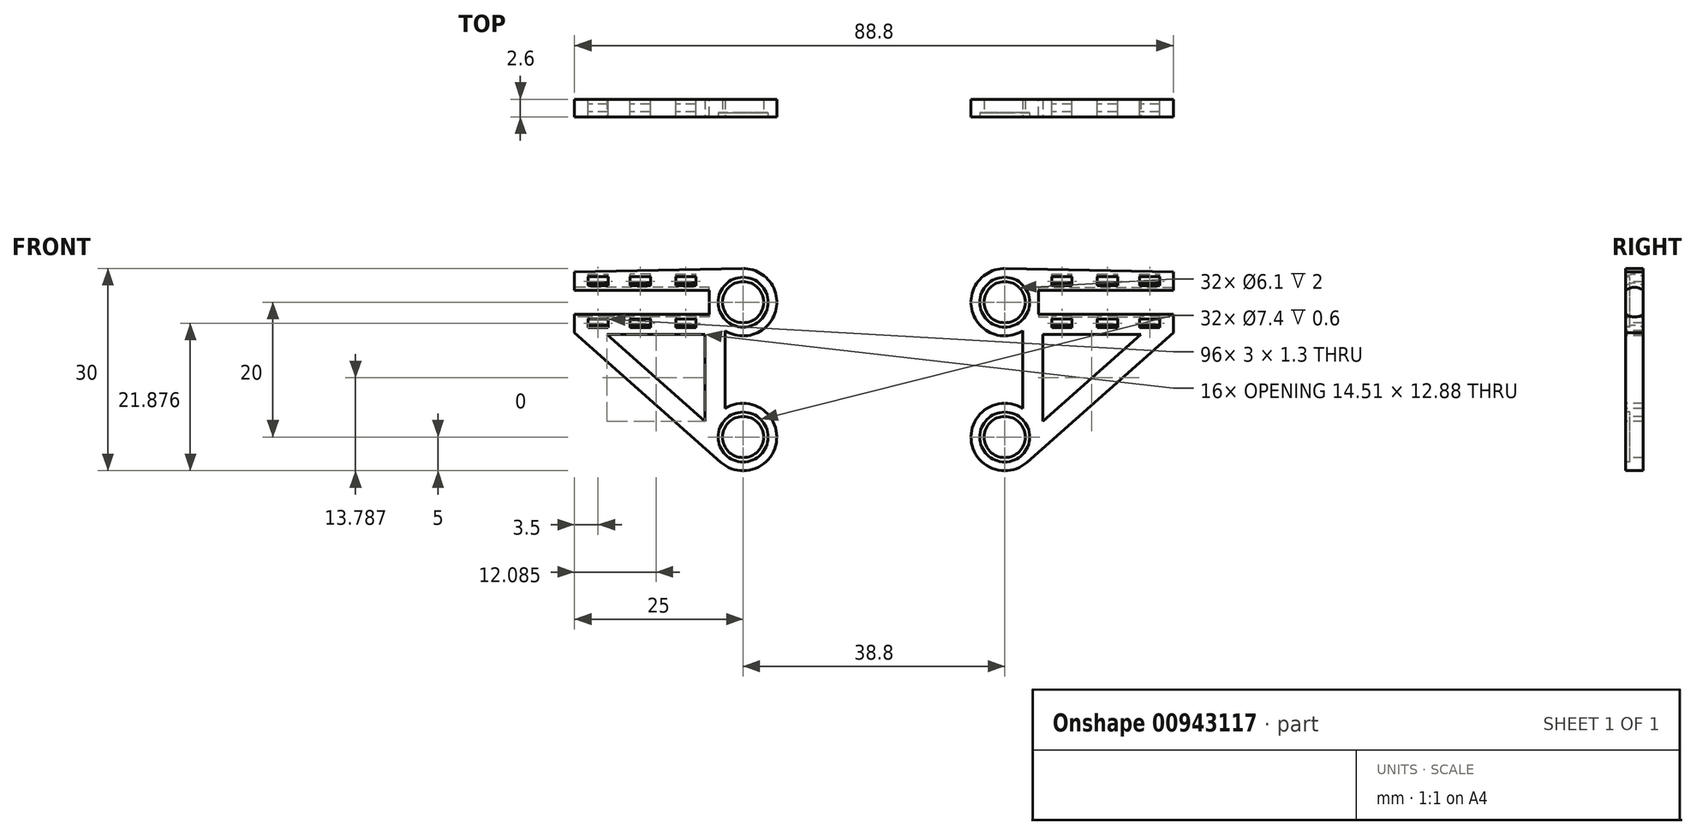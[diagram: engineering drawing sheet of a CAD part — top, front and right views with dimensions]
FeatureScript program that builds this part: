
annotation { "Feature Type Name" : "Feature", "Feature Type Description" : "" }
export const myFeature = defineFeature(function(context is Context, id is Id, definition is map)
    precondition{}
    {
        {
            var Q0;
            Q0=qCreatedBy(makeId("Front.planeOp"),FACE);
            var sketch = newSketch(context, id + "F0", { "sketchPlane" : qUnion([Q0])});
            skLineSegment(sketch, "E0", {"start": v(0.1, 5) * mm, "end": v(25, 4.5) * mm});
            skLineSegment(sketch, "E1", {"start": v(25, 4.5) * mm, "end": v(25, -4.5) * mm});
            skLineSegment(sketch, "E2", {"start": v(25, -4.5) * mm, "end": v(3.32, -23.74) * mm});
            skPoint(sketch, "E3", {"position": v(0, 0) * mm});
            skPoint(sketch, "E4", {"position": v(0, -20) * mm});
            skLineSegment(sketch, "E5", {"start": v(0, 0) * mm, "end": v(25, 0) * mm, "construction": true});
            skArc(sketch, "E6.filletArc", {"start": v(2.66, -15.77) * mm, "mid": v(-4.98, -20.41) * mm, "end": v(3.32, -23.74) * mm});
            skArc(sketch, "E7.filletArc", {"start": v(0.1, 5) * mm, "mid": v(-4.82, -1.34) * mm, "end": v(2.66, -4.23) * mm});
            skLineSegment(sketch, "E8", {"start": v(2.66, -4.23) * mm, "end": v(2.66, -15.77) * mm});
            skSolve(sketch);
        }
        {
            var Q0;
            Q0=makeQuery(id+"F0.imprint","IMPRINT",FACE,{"disambiguationData":[TD([[makeQuery(id+"F0.imprint","IMPRINT",EDGE,{"derivedFrom":sQuery(id+"F0.wireOp",EDGE,"E0")}),-1.0]])]});
            extrude(context, id + "F1", {"entities" : qUnion([Q0]), "oppositeDirection" : true, "depth" : 2.6 * mm, "offsetDistance" : 25 * mm});
        }
        {
            var Q0;
            Q0=sQuery(id+"F0.wireOp",VERTEX,"E3");
            var Q1;
            Q1=sQuery(id+"F0.wireOp",VERTEX,"E4");
            var Q2;
            Q2=makeQuery(id+"F1.opExtrude","SWEPT_BODY",BODY,{"disambiguationData":[OSD([sQuery(id+"F0.wireOp",EDGE,"RJbdalpD-36lB-MyLH-ccrA-Tx8w9Rtr1OP7"),sQuery(id+"F0.wireOp",EDGE,"E0"),sQuery(id+"F0.wireOp",EDGE,"E1"),sQuery(id+"F0.wireOp",EDGE,"E2"),sQuery(id+"F0.wireOp",EDGE,"E6.filletArc"),sQuery(id+"F0.wireOp",EDGE,"E7.filletArc")])]});
            hole(context, id + "F2", {"style" : HoleStyle.C_BORE, "endStyle" : HoleEndStyle.BLIND, "holeDiameter" : 6.1 * mm, "cBoreDiameter" : 7.4 * mm, "cBoreDepth" : 0.6 * mm, "majorDiameter" : 5 * mm, "holeDepth" : 3 * mm, "isTappedThrough" : true, "tappedDepth" : 12 * mm, "tapClearance" : 3, "startFromSketch" : true, "locations" : qUnion([Q0, Q1]), "scope" : qUnion([Q2])});
        }
        {
            var Q0;
            Q0=makeQuery(id+"F1.opExtrude","SWEPT_FACE",FACE,{"disambiguationData":[OSD([sQuery(id+"F0.wireOp",EDGE,"E1")])]});
            var sketch = newSketch(context, id + "F3", { "sketchPlane" : qUnion([Q0])});
            skCircle(sketch, "E9", {"center": v(1.3, 0) * mm, "radius": 2.2 * mm});
            skPoint(sketch, "E9.centerSnap0", {"position": v(1.3, 4.5) * mm});
            skPoint(sketch, "E9.centerSnap1", {"position": v(2.6, 0) * mm});
            skSolve(sketch);
        }
        {
            var Q0;
            Q0=qSketchRegion(id+"F3",true);
            extrude(context, id + "F4", {"entities" : qUnion([Q0]), "operationType" : NewBodyOperationType.REMOVE, "oppositeDirection" : true, "depth" : 20 * mm, "offsetDistance" : 25 * mm});
        }
        {
            var Q0;
            Q0=qCreatedBy(makeId("Front.planeOp"),FACE);
            var sketch = newSketch(context, id + "F5", { "sketchPlane" : qUnion([Q0])});
            skLineSegment(sketch, "E10", {"start": v(5.66, -4.77) * mm, "end": v(5.66, -17.65) * mm});
            skLineSegment(sketch, "E11", {"start": v(5.66, -17.65) * mm, "end": v(20.17, -4.77) * mm});
            skLineSegment(sketch, "E12", {"start": v(20.17, -4.77) * mm, "end": v(5.66, -4.77) * mm});
            skSolve(sketch);
        }
        {
            var Q0;
            Q0=qSketchRegion(id+"F5",true);
            extrude(context, id + "F6", {"entities" : qUnion([Q0]), "operationType" : NewBodyOperationType.REMOVE, "oppositeDirection" : true, "depth" : 25 * mm, "offsetDistance" : 25 * mm});
        }
        {
            var Q0;
            Q0=makeQuery(id+"F1.opExtrude","CAP_FACE",FACE,{"disambiguationData":[OSD([sQuery(id+"F0.wireOp",EDGE,"E0"),sQuery(id+"F0.wireOp",EDGE,"E1"),sQuery(id+"F0.wireOp",EDGE,"E2"),sQuery(id+"F0.wireOp",EDGE,"E6.filletArc"),sQuery(id+"F0.wireOp",EDGE,"E7.filletArc"),sQuery(id+"F0.wireOp",EDGE,"E8")])],"isStart":true});
            var sketch = newSketch(context, id + "F7", { "sketchPlane" : qUnion([Q0])});
            skLineSegment(sketch, "E13.bottom", {"start": v(20, 3.77) * mm, "end": v(23, 3.77) * mm});
            skLineSegment(sketch, "E13.top", {"start": v(20, 2.47) * mm, "end": v(23, 2.47) * mm});
            skLineSegment(sketch, "E13.left", {"start": v(20, 3.77) * mm, "end": v(20, 2.47) * mm});
            skLineSegment(sketch, "E13.right", {"start": v(23, 3.77) * mm, "end": v(23, 2.47) * mm});
            skLineSegment(sketch, "E14.bottom", {"start": v(7, 3.77) * mm, "end": v(10, 3.77) * mm});
            skLineSegment(sketch, "E14.top", {"start": v(7, 2.47) * mm, "end": v(10, 2.47) * mm});
            skLineSegment(sketch, "E14.left", {"start": v(7, 3.77) * mm, "end": v(7, 2.47) * mm});
            skLineSegment(sketch, "E14.right", {"start": v(10, 3.77) * mm, "end": v(10, 2.47) * mm});
            skLineSegment(sketch, "E15.bottom", {"start": v(7, -2.47) * mm, "end": v(10, -2.47) * mm});
            skLineSegment(sketch, "E15.top", {"start": v(7, -3.77) * mm, "end": v(10, -3.77) * mm});
            skLineSegment(sketch, "E15.left", {"start": v(7, -2.47) * mm, "end": v(7, -3.77) * mm});
            skLineSegment(sketch, "E15.right", {"start": v(10, -2.47) * mm, "end": v(10, -3.77) * mm});
            skLineSegment(sketch, "E16.bottom", {"start": v(20, -2.47) * mm, "end": v(23, -2.47) * mm});
            skLineSegment(sketch, "E16.top", {"start": v(20, -3.77) * mm, "end": v(23, -3.77) * mm});
            skLineSegment(sketch, "E16.left", {"start": v(20, -2.47) * mm, "end": v(20, -3.77) * mm});
            skLineSegment(sketch, "E16.right", {"start": v(23, -2.47) * mm, "end": v(23, -3.77) * mm});
            skLineSegment(sketch, "E17.bottom", {"start": v(13.74, 3.77) * mm, "end": v(16.74, 3.77) * mm});
            skLineSegment(sketch, "E17.top", {"start": v(13.74, 2.47) * mm, "end": v(16.74, 2.47) * mm});
            skLineSegment(sketch, "E17.left", {"start": v(13.74, 3.77) * mm, "end": v(13.74, 2.47) * mm});
            skLineSegment(sketch, "E17.right", {"start": v(16.74, 3.77) * mm, "end": v(16.74, 2.47) * mm});
            skLineSegment(sketch, "E18.bottom", {"start": v(13.74, -2.47) * mm, "end": v(16.74, -2.47) * mm});
            skLineSegment(sketch, "E18.top", {"start": v(13.74, -3.77) * mm, "end": v(16.74, -3.77) * mm});
            skLineSegment(sketch, "E18.left", {"start": v(13.74, -2.47) * mm, "end": v(13.74, -3.77) * mm});
            skLineSegment(sketch, "E18.right", {"start": v(16.74, -2.47) * mm, "end": v(16.74, -3.77) * mm});
            skSolve(sketch);
        }
        {
            var Q0;
            Q0=makeQuery(id+"F7.imprint","IMPRINT",FACE,{"disambiguationData":[TD([[makeQuery(id+"F7.imprint","IMPRINT",EDGE,{"derivedFrom":sQuery(id+"F7.wireOp",EDGE,"E14.bottom")}),-1.0]])]});
            var Q1;
            Q1=makeQuery(id+"F7.imprint","IMPRINT",FACE,{"disambiguationData":[TD([[makeQuery(id+"F7.imprint","IMPRINT",EDGE,{"derivedFrom":sQuery(id+"F7.wireOp",EDGE,"E17.bottom")}),-1.0]])]});
            var Q2;
            Q2=makeQuery(id+"F7.imprint","IMPRINT",FACE,{"disambiguationData":[TD([[makeQuery(id+"F7.imprint","IMPRINT",EDGE,{"derivedFrom":sQuery(id+"F7.wireOp",EDGE,"E13.bottom")}),-1.0]])]});
            var Q3;
            Q3=makeQuery(id+"F4.boolean.opBoolean","COPY",EDGE,{"disambiguationData":[OD(0.0)],"derivedFrom":makeQuery(id+"F4.opExtrude","CAP_EDGE",EDGE,{"disambiguationData":[OSD([sQuery(id+"F3.wireOp",EDGE,"E9")])],"isStart":true})});
            sweep(context, id + "F8", {"operationType" : NewBodyOperationType.REMOVE, "profiles" : qUnion([Q0, Q1, Q2]), "path" : qUnion([Q3]), "keepProfileOrientation" : true});
        }
        {
            var Q0;
            Q0=makeQuery(id+"F7.imprint","IMPRINT",FACE,{"disambiguationData":[TD([[makeQuery(id+"F7.imprint","IMPRINT",EDGE,{"derivedFrom":sQuery(id+"F7.wireOp",EDGE,"E15.bottom")}),-1.0]])]});
            var Q1;
            Q1=makeQuery(id+"F7.imprint","IMPRINT",FACE,{"disambiguationData":[TD([[makeQuery(id+"F7.imprint","IMPRINT",EDGE,{"derivedFrom":sQuery(id+"F7.wireOp",EDGE,"E18.bottom")}),-1.0]])]});
            var Q2;
            Q2=makeQuery(id+"F7.imprint","IMPRINT",FACE,{"disambiguationData":[TD([[makeQuery(id+"F7.imprint","IMPRINT",EDGE,{"derivedFrom":sQuery(id+"F7.wireOp",EDGE,"E16.bottom")}),-1.0]])]});
            var Q3;
            Q3=makeQuery(id+"F4.boolean.opBoolean","COPY",EDGE,{"disambiguationData":[OD(1.0)],"derivedFrom":makeQuery(id+"F4.opExtrude","CAP_EDGE",EDGE,{"disambiguationData":[OSD([sQuery(id+"F3.wireOp",EDGE,"E9")])],"isStart":true})});
            sweep(context, id + "F9", {"operationType" : NewBodyOperationType.REMOVE, "profiles" : qUnion([Q0, Q1, Q2]), "path" : qUnion([Q3]), "keepProfileOrientation" : true});
        }
        {
            var Q0;
            Q0=qCreatedBy(makeId("Right.planeOp"),FACE);
            cPlane(context, id + "F10", {"entities" : qUnion([Q0]), "cplaneType" : CPlaneType.OFFSET, "offset" : 19.4 * mm, "oppositeDirection" : true, "width" : 150 * mm, "height" : 150 * mm});
        }
        {
            var Q0;
            Q0=makeQuery(id+"F1.opExtrude","SWEPT_BODY",BODY,{"disambiguationData":[OSD([sQuery(id+"F0.wireOp",EDGE,"RJbdalpD-36lB-MyLH-ccrA-Tx8w9Rtr1OP7"),sQuery(id+"F0.wireOp",EDGE,"E0"),sQuery(id+"F0.wireOp",EDGE,"E1"),sQuery(id+"F0.wireOp",EDGE,"E2"),sQuery(id+"F0.wireOp",EDGE,"E6.filletArc"),sQuery(id+"F0.wireOp",EDGE,"E7.filletArc")])]});
            var Q1;
            Q1=qCreatedBy(id+"F10.planeOp",FACE);
            mirror(context, id + "F11", {"entities" : qUnion([Q0]), "mirrorPlane" : qUnion([Q1])});
        }
    });
